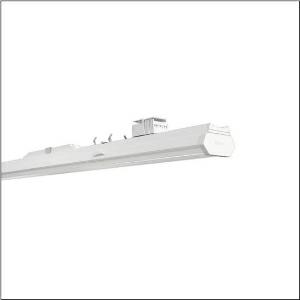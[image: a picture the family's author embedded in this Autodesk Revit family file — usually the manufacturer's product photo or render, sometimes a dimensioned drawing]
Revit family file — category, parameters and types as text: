
# Revit family: licross_r__11_protected_mo_51td12mn4axg_dbc1
name_source: partatom
category: Lighting Fixtures
units: mm (PartAtom-declared; Revit-internal decimal feet)

## family parameters
Cut with Voids When Loaded = No
Host = Face
Light Source = No
Part Type = Normal
Room Calculation Point = No
Round Connector Dimension = Use Diameter
Shared = No

## types (1)
- --- (1 x LED, 10020 lm, 55.3 W, 4000K)
    Apparent Load = 55 VA
    CIE Flux Codes = 73 92 98 99 100
    Color Rendering = 80
    Color Temperature = 4000K
    Default Elevation = 1800 mm
    Description = Licross® 11 Protected MO, luminaire insert, of sheet steel, galvanised, coil coated, white, length: 1.500mm, width: 90mm, height: 101mm, LED rated luminous flux: 10.030lm, light colour: 840, control gear: ON/OFF Multilumen, with plug, 3-pole, with phase selection, mains connection: 220..240V, AC, 50/60Hz, rated input power: 55W, internal wiring halogen-free, primary light control with lens, of plastic, primary optical cover: cover, of PMMA, light emission: direct distribution, primary light characteristic: symmetric, protection rating (complete): IP54, insulation class (complete): insulation class I (protective earthing), certification: CE, ENEC, VDE, UKCA, protection symbol: D if used in an environment with non-conductive dust loads with corresponding accessories, impact resistance: IK06, permissible ambient temperature for indoor applications: -35..+40°C, corresponds to IFS (International Featured Standards) requirements for safety and quality in the food industry, reducing of maximum allowable ambient temperature of 5°C with ceiling mounting, LABS conformity tested according to VDMA 24364:2018-05, packaging unit: 1 piece
    Height = 92 mm
    Lamp = 1 x LED
    Lamp Light Flux = 10020 lm
    Lamp Power = 55.3 W
    Lamp count = 1
    Length = 1500 mm
    Luminous efficacy = 181 lm/W
    Manufacturer = Siteco
    ModVariant = No
    Model = 51TD12MN4AXG
    Mounting Place = Ceiling
    Mounting Type = Pendant
    Number of Poles = 1
    OnlyDefault = Yes
    Power Factor = 1
    Product Name = Licross® 11 Protected MO
    Product group = luminaire insert | ceiling pendant
    ProductGroupID = 902
    Protection Class = Protection class I
    Protection Degree = IP 54
    RLX_Detail_Level = 1
    RLX_Emergency_Light_Flux = 0 lm
    RLX_Emergency_Type = 0
    RLX_Emergency_Type_DB = No
    RlxData = <blob elided: 22181 chars, md5=4a68756c>
    Socket = socket
    Standby Power = 0 W
    System Light Flux = 10020 lm
    System Power = 55 W
    Type Comments = factory setting: luminous flux: 100 % | (A | C | E) | 126 mA
    Type Image = l_1256145.jpg
    URL = http://relux.com
    VarID = @adj_107441
    Voltage = 0 V
    Weight = 0.00 kg
    Width = 88 mm

## geometry (parser evidence)
native form markers: Blend x4, Sweep x11
no freeform markers — native parametric forms only
